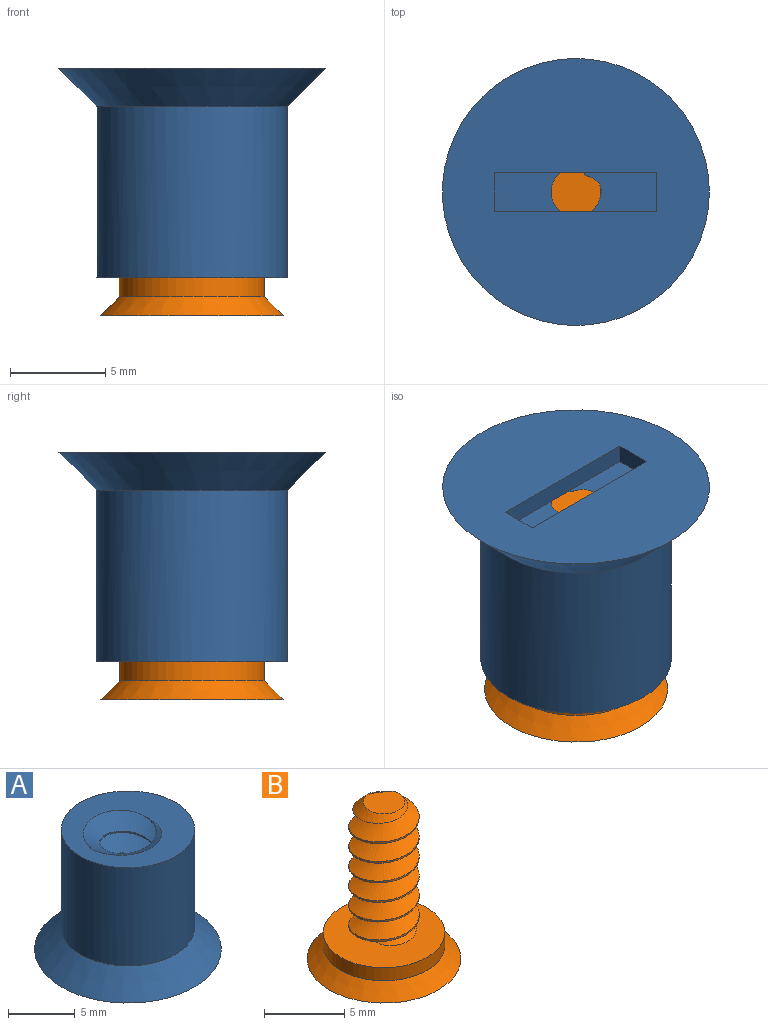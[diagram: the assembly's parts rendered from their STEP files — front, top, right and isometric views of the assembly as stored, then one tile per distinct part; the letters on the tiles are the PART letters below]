
ASSEMBLY  parts=2 mates=1
PART A: 14 faces, bbox 15.2x15.2x13.5 mm
  f0: bspline ~11x8.64mm, area 152.7mm2, adj f1,f4,f5,f6,f13
  f1: bspline ~11x8.64mm, area 152.4mm2, adj f0,f4,f5,f6,f13
  f2: plane 14x14mm, normal (0,0,-1), area 136.9mm2, adj f7,f8,f9,f10,f11
  f3: cylinder r=5mm len=10mm, axis (0,0,-1), area 282.7mm2, adj f4,f7
  f4: plane 11.16x11.16mm, normal (0,0,1), area 51.7mm2, adj f0,f1,f3,f13
  f5: cone r=3.02mm half-angle=45deg, axis (0,0,-1), area 6.9mm2, adj f0,f1,f6,f13
  f6: plane 7.04x6.32mm, normal (0,0,1), area 31.7mm2, adj f0,f1,f5
  f7: cone r=7mm half-angle=45deg, axis (0,0,-1), area 106.6mm2, adj f2,f3
  f8: plane 8.5x1mm, normal (0,1,0), area 8.5mm2, adj f2,f9,f11,f12
  f9: plane 2x1mm, normal (1,0,0), area 2mm2, adj f2,f8,f10,f12
  f10: plane 8.5x1mm, normal (0,-1,0), area 8.5mm2, adj f2,f9,f11,f12
  f11: plane 2x1mm, normal (-1,0,0), area 2mm2, adj f2,f8,f10,f12
  f12: plane 8.5x2mm, normal (0,0,-1), area 17mm2, adj f8,f9,f10,f11
  f13: cylinder r=2.12mm len=8.1mm, axis (0,0,1), area 7.7mm2, adj f0,f1,f4,f5
PART B: 14 faces, bbox 9.7x9.7x12.8 mm
  f0: cone r=1.3mm half-angle=45deg, axis (0,0,-1), area 5.6mm2, adj f1,f2,f4,f13
  f1: bspline ~11.5x5.31mm, area 88.1mm2, adj f0,f2,f4,f6,f13
  f2: bspline ~11.25x5.31mm, area 89.4mm2, adj f0,f1,f4,f6,f13
  f3: plane 9.6x9.6mm, normal (0,0,-1), area 60.2mm2, adj f7,f8,f9,f10,f11
  f4: plane 2.67x2.65mm, normal (0,0,1), area 5.1mm2, adj f0,f1,f2
  f5: cylinder r=3.8mm len=7.6mm, axis (0,0,1), area 23.9mm2, adj f6,f7
  f6: plane 7.6x7.6mm, normal (0,0,1), area 36.3mm2, adj f1,f2,f5,f13
  f7: cone r=4.8mm half-angle=45deg, axis (0,0,-1), area 38.2mm2, adj f3,f5
  f8: plane 6.1x1mm, normal (0,1,0), area 6.1mm2, adj f3,f9,f11,f12
  f9: plane 2x1mm, normal (1,0,0), area 2mm2, adj f3,f8,f10,f12
  f10: plane 6.1x1mm, normal (0,-1,0), area 6.1mm2, adj f3,f9,f11,f12
  f11: plane 2x1mm, normal (-1,0,0), area 2mm2, adj f3,f8,f10,f12
  f12: plane 6.1x2mm, normal (0,0,-1), area 12.2mm2, adj f8,f9,f10,f11
  f13: cylinder r=2.2mm len=9.1mm, axis (0,0,1), area 12.5mm2, adj f0,f1,f2,f6
PLACE A rot(axis=(0,1,0),180deg) t=(-0.42,0.12,8.99)mm
PLACE B t=(-0.42,0.12,0)mm
MATE slider A.f3 <-> B.f5  axis (0,0,1) through (-0.42,0.12,-0.01)mm
